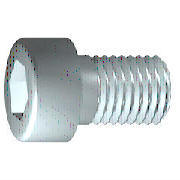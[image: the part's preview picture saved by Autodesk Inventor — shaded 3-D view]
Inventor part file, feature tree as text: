
AUTODESK INVENTOR PART (.ipt)
format: ipt  version: 2020 (Build 240168000, 168)  size: 201,216 bytes
history: native  units: mm (DEFAULTED — no unit token found)
features: sketch x2, other x1, extrude x1, plane x1, fillet x1
ambient origin geometry x7: Origin, YZ Plane, XY Plane, X Axis, Y Axis, Z Axis, Center Point
bodies: Solid1 (feature_tree)
feature tree (6):
  other  "Bryła"
  extrude  "Szczelina"  Depth=7.0mm
  plane  "Work Plane1"
  fillet  "Fillet2"  Radius=0.61355mm
  sketch  "Szkic1"
  sketch  "Szkic2"
